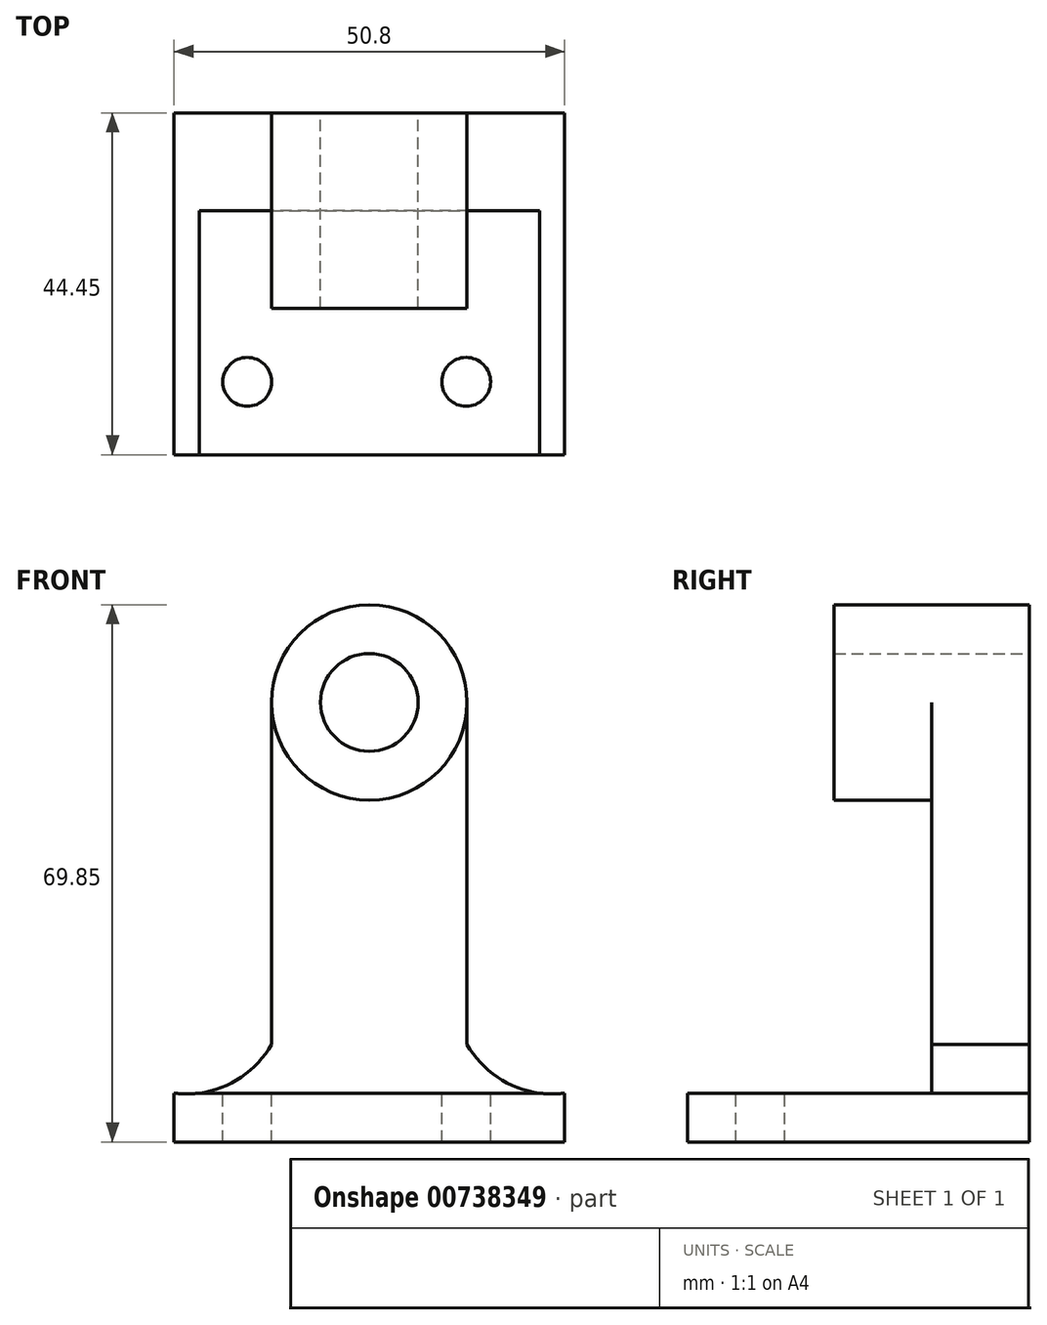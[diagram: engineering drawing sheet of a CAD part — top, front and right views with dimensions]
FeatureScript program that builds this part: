
annotation { "Feature Type Name" : "Feature", "Feature Type Description" : "" }
export const myFeature = defineFeature(function(context is Context, id is Id, definition is map)
    precondition{}
    {
        {
            var Q0;
            Q0=qCreatedBy(makeId("Right.planeOp"),FACE);
            var sketch = newSketch(context, id + "F0", { "sketchPlane" : qUnion([Q0])});
            skLineSegment(sketch, "E0", {"start": v(0, 0) * mm, "end": v(0, 69.85) * mm});
            skLineSegment(sketch, "E1", {"start": v(0, 69.85) * mm, "end": v(-12.7, 69.85) * mm});
            skLineSegment(sketch, "E2", {"start": v(-12.7, 69.85) * mm, "end": v(-12.7, 6.35) * mm});
            skLineSegment(sketch, "E3", {"start": v(-12.7, 6.35) * mm, "end": v(-44.45, 6.35) * mm});
            skLineSegment(sketch, "E4", {"start": v(-44.45, 6.35) * mm, "end": v(-44.45, 0) * mm});
            skLineSegment(sketch, "E5", {"start": v(-44.45, 0) * mm, "end": v(0, 0) * mm});
            skSolve(sketch);
        }
        {
            var Q0;
            Q0 = qSketchRegion(id + "F0", true);
            extrude(context, id + "F1", {"entities" : qUnion([Q0]), "depth" : 50.8 * mm, "offsetDistance" : 25.4 * mm});
        }
        {
            var Q0;
            Q0=makeQuery(id+"F1.opExtrude","SWEPT_FACE",FACE,{"disambiguationData":[OSD([sQuery(id+"F0.wireOp",EDGE,"E2")])]});
            var sketch = newSketch(context, id + "F2", { "sketchPlane" : qUnion([Q0])});
            skLineSegment(sketch, "E6", {"start": v(0, 69.85) * mm, "end": v(25.4, 69.85) * mm});
            skLineSegment(sketch, "E7", {"start": v(25.4, 69.85) * mm, "end": v(25.4, 57.15) * mm});
            skCircle(sketch, "E8", {"center": v(25.4, 57.15) * mm, "radius": 6.35 * mm});
            skCircle(sketch, "E9", {"center": v(25.4, 57.15) * mm, "radius": 12.7 * mm});
            skSolve(sketch);
        }
        {
            var Q0;
            Q0=makeQuery(id+"F2.imprint","IMPRINT",FACE,{"disambiguationData":[TD([[makeQuery(id+"F2.imprint","IMPRINT",EDGE,{"derivedFrom":sQuery(id+"F2.wireOp",EDGE,"E8")}),-1.0]])]});
            extrude(context, id + "F3", {"entities" : qUnion([Q0]), "operationType" : NewBodyOperationType.ADD, "depth" : 12.7 * mm, "offsetDistance" : 25.4 * mm});
        }
        {
            var Q0;
            Q0=makeQuery(id+"F1.opExtrude","SWEPT_FACE",FACE,{"disambiguationData":[OSD([sQuery(id+"F0.wireOp",EDGE,"E0")])]});
            var sketch = newSketch(context, id + "F4", { "sketchPlane" : qUnion([Q0])});
            skLineSegment(sketch, "E10", {"start": v(-25.4, 69.85) * mm, "end": v(-25.4, 57.15) * mm});
            skCircle(sketch, "E11", {"center": v(-25.4, 57.15) * mm, "radius": 6.35 * mm});
            skCircle(sketch, "E12", {"center": v(-25.4, 57.15) * mm, "radius": 12.7 * mm});
            skLineSegment(sketch, "E13", {"start": v(-38.1, 57.15) * mm, "end": v(-38.1, 12.7) * mm});
            skLineSegment(sketch, "E14", {"start": v(-12.7, 57.15) * mm, "end": v(-12.7, 12.7) * mm});
            skLineSegment(sketch, "E15", {"start": v(-38.1, 12.7) * mm, "end": v(-50.8, 12.7) * mm});
            skLineSegment(sketch, "E16", {"start": v(-50.8, 12.7) * mm, "end": v(-50.8, 6.35) * mm});
            skArc(sketch, "E17", {"start": v(-50.8, 6.35) * mm, "mid": v(-43.48, 7.58) * mm, "end": v(-38.1, 12.7) * mm});
            skArc(sketch, "E18", {"start": v(-12.7, 12.7) * mm, "mid": v(-7.32, 7.58) * mm, "end": v(0, 6.35) * mm});
            skSolve(sketch);
        }
        {
            var Q0;
            Q0=makeQuery(id+"F1.opExtrude","SWEPT_FACE",FACE,{"disambiguationData":[OSD([sQuery(id+"F0.wireOp",EDGE,"E3")])]});
            var sketch = newSketch(context, id + "F5", { "sketchPlane" : qUnion([Q0])});
            skLineSegment(sketch, "E19", {"start": v(0, -44.53) * mm, "end": v(0, -34.98) * mm});
            skLineSegment(sketch, "E20", {"start": v(0, -34.98) * mm, "end": v(9.52, -34.98) * mm});
            skCircle(sketch, "E21", {"center": v(9.52, -34.98) * mm, "radius": 3.18 * mm});
            skLineSegment(sketch, "E22", {"start": v(47.52, -34.98) * mm, "end": v(38, -34.98) * mm});
            skCircle(sketch, "E23", {"center": v(38, -34.98) * mm, "radius": 3.18 * mm});
            skSolve(sketch);
        }
        {
            var Q0;
            Q0=makeQuery(id+"F5.imprint","IMPRINT",FACE,{"disambiguationData":[TD([[makeQuery(id+"F5.imprint","IMPRINT",EDGE,{"derivedFrom":sQuery(id+"F5.wireOp",EDGE,"E21")}),1.0]])]});
            var Q1;
            Q1=makeQuery(id+"F5.imprint","IMPRINT",FACE,{"disambiguationData":[TD([[makeQuery(id+"F5.imprint","IMPRINT",EDGE,{"derivedFrom":sQuery(id+"F5.wireOp",EDGE,"E23")}),1.0]])]});
            extrude(context, id + "F6", {"entities" : qUnion([Q0, Q1]), "operationType" : NewBodyOperationType.REMOVE, "endBound" : BoundingType.THROUGH_ALL, "oppositeDirection" : true, "depth" : 25.4 * mm, "offsetDistance" : 25.4 * mm});
        }
        {
            var Q0;
            Q0=makeQuery(id+"F1.opExtrude","SWEPT_FACE",FACE,{"disambiguationData":[OSD([sQuery(id+"F0.wireOp",EDGE,"E3")])]});
            var sketch = newSketch(context, id + "F7", { "sketchPlane" : qUnion([Q0])});
            skLineSegment(sketch, "E24", {"start": v(9.52, -34.98) * mm, "end": v(0, -34.98) * mm});
            skLineSegment(sketch, "E25", {"start": v(0, -34.98) * mm, "end": v(0, -44.44) * mm});
            skLineSegment(sketch, "E26", {"start": v(9.52, -34.98) * mm, "end": v(9.53, -44.45) * mm});
            skArc(sketch, "E27", {"start": v(0, -34.98) * mm, "mid": v(2.8, -41.7) * mm, "end": v(9.53, -44.45) * mm});
            skLineSegment(sketch, "E28", {"start": v(38, -34.98) * mm, "end": v(50.83, -34.98) * mm});
            skLineSegment(sketch, "E29", {"start": v(38, -34.98) * mm, "end": v(38, -44.45) * mm});
            skSolve(sketch);
        }
        {
            var Q0;
            {var subQ0=sQuery(id+"F7.wireOp",EDGE,"E27");var subQ1=makeQuery(id+"F1.opExtrude","SWEPT_EDGE",EDGE,{"disambiguationData":[OSD([sQuery(id+"F0.wireOp",EDGE,"E3"),sQuery(id+"F0.wireOp",EDGE,"E4")])]});var subQ3=makeQuery(id+"F7.imprint","INTERSECT",VERTEX,{"derivedFrom":[subQ1,subQ0]});Q0=makeQuery(id+"F7.imprint","IMPRINT",FACE,{"disambiguationData":[TD([[makeQuery(id+"F7.imprint","IMPRINT",EDGE,{"disambiguationData":[TD([[subQ3,-1.0]])],"derivedFrom":subQ0}),1.0]])]});}
            var Q1;
            {var subQ0=sQuery(id+"F7.wireOp",EDGE,"E26");var subQ1=sQuery(id+"F7.wireOp",EDGE,"E24");var subQ2=makeQuery(id+"F7.imprint","INTERSECT",VERTEX,{"derivedFrom":[subQ1,subQ0]});Q1=makeQuery(id+"F7.imprint","IMPRINT",FACE,{"disambiguationData":[TD([[makeQuery(id+"F7.imprint","IMPRINT",EDGE,{"disambiguationData":[TD([[subQ2,-1.0]])],"derivedFrom":subQ1}),1.0]])]});}
            var Q2;
            {var subQ0=sQuery(id+"F7.wireOp",EDGE,"E27");var subQ1=sQuery(id+"F0.wireOp",EDGE,"E3");var subQ2=makeQuery(id+"FrQkuHLKhcuPX5Z_1.boolean.opBoolean","INTERSECT",EDGE,{"derivedFrom":[makeQuery(id+"F1.opExtrude","SWEPT_FACE",FACE,{"disambiguationData":[OSD([subQ1])]}),makeQuery(id+"FrQkuHLKhcuPX5Z_1.opExtrude","SWEPT_FACE",FACE,{"disambiguationData":[OSD([sQuery(id+"F4.wireOp",EDGE,"E18")])]})]});var subQ3=makeQuery(id+"F7.imprint","INTERSECT",VERTEX,{"derivedFrom":[subQ2,subQ0]});Q2=makeQuery(id+"F7.imprint","IMPRINT",FACE,{"disambiguationData":[TD([[makeQuery(id+"F7.imprint","IMPRINT",EDGE,{"disambiguationData":[TD([[subQ3,-1.0]])],"derivedFrom":subQ0}),-1.0]])]});}
            extrude(context, id + "F8", {"entities" : qUnion([Q0, Q1, Q2]), "operationType" : NewBodyOperationType.REMOVE, "endBound" : BoundingType.THROUGH_ALL, "oppositeDirection" : true, "depth" : 25.4 * mm, "offsetDistance" : 25.4 * mm});
        }
        {
            var Q0;
            Q0=makeQuery(id+"F4.imprint","IMPRINT",FACE,{"disambiguationData":[TD([[makeQuery(id+"F4.imprint","IMPRINT",EDGE,{"derivedFrom":sQuery(id+"F4.wireOp",EDGE,"E15")}),1.0]])]});
            var Q1;
            {var subQ1=sQuery(id+"F4.wireOp",EDGE,"E13");Q1=makeQuery(id+"F4.imprint","IMPRINT",FACE,{"disambiguationData":[TD([[makeQuery(id+"F4.imprint","IMPRINT",EDGE,{"derivedFrom":subQ1}),-1.0]])]});}
            var Q2;
            {var subQ1=sQuery(id+"F4.wireOp",EDGE,"E14");Q2=makeQuery(id+"F4.imprint","IMPRINT",FACE,{"disambiguationData":[TD([[makeQuery(id+"F4.imprint","IMPRINT",EDGE,{"derivedFrom":subQ1}),1.0]])]});}
            var Q3;
            Q3=makeQuery(id+"F4.imprint","IMPRINT",FACE,{"disambiguationData":[TD([[makeQuery(id+"F4.imprint","IMPRINT",EDGE,{"derivedFrom":sQuery(id+"F4.wireOp",EDGE,"E11")}),1.0]])]});
            extrude(context, id + "F9", {"entities" : qUnion([Q0, Q1, Q2, Q3]), "operationType" : NewBodyOperationType.REMOVE, "endBound" : BoundingType.THROUGH_ALL, "oppositeDirection" : true, "depth" : 25.4 * mm, "offsetDistance" : 25.4 * mm});
        }
    });
